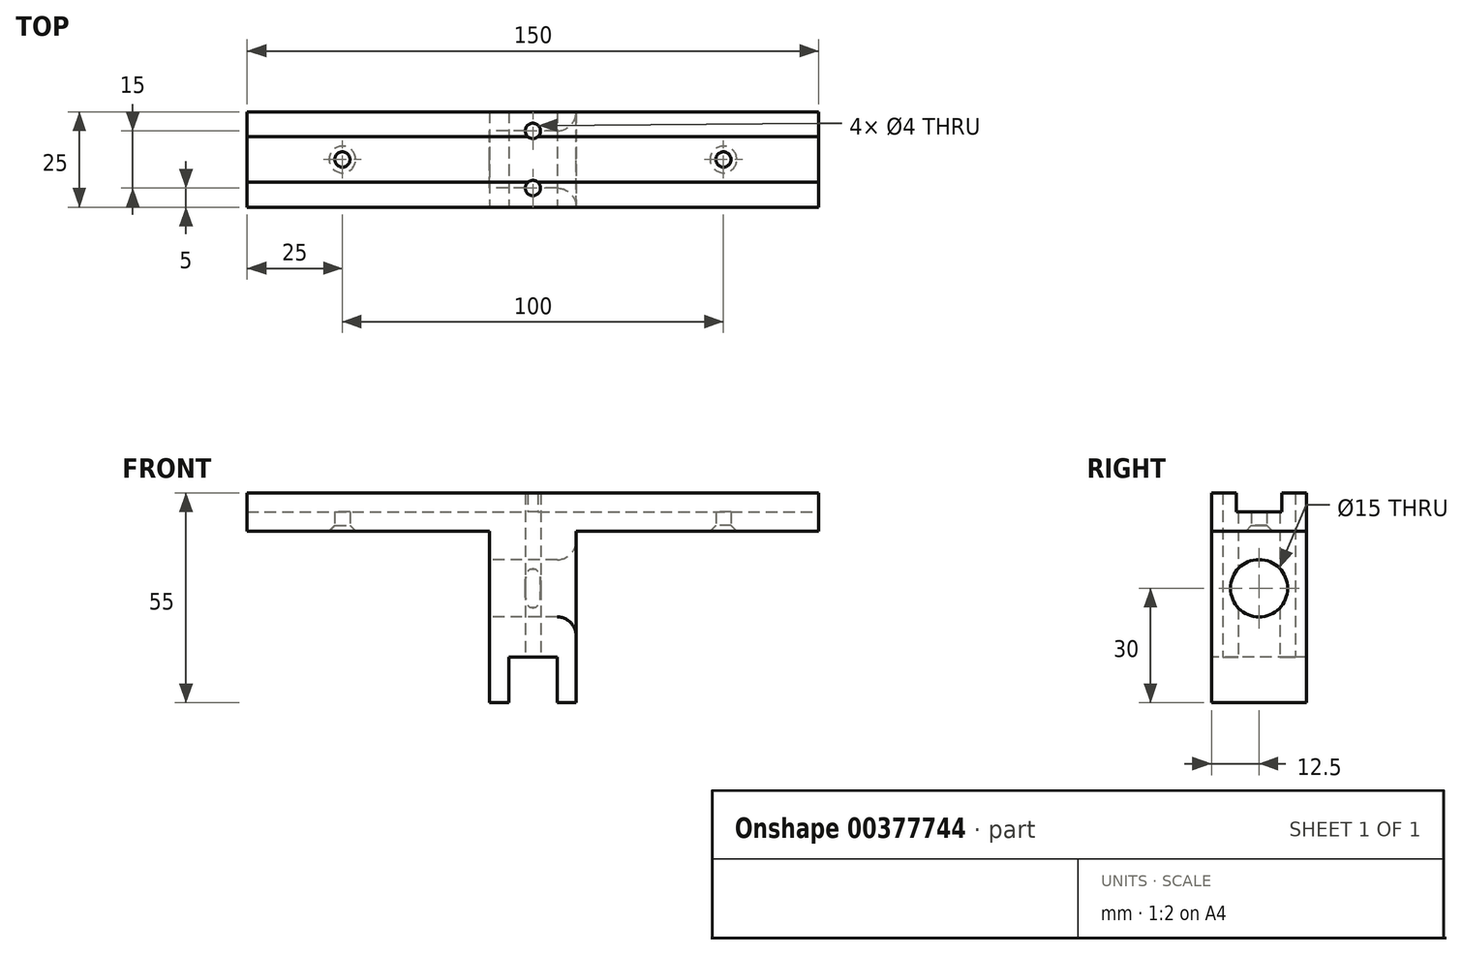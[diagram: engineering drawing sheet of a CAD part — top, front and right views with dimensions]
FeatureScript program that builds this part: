
annotation { "Feature Type Name" : "Feature", "Feature Type Description" : "" }
export const myFeature = defineFeature(function(context is Context, id is Id, definition is map)
    precondition{}
    {
        {
            var Q0;
            Q0=qCreatedBy(makeId("Top.planeOp"),FACE);
            var sketch = newSketch(context, id + "F0", { "sketchPlane" : qUnion([Q0])});
            skLineSegment(sketch, "E0.bottom", {"start": v(75, -12.5) * mm, "end": v(-75, -12.5) * mm});
            skLineSegment(sketch, "E0.top", {"start": v(75, 12.5) * mm, "end": v(-75, 12.5) * mm});
            skLineSegment(sketch, "E0.left", {"start": v(75, -12.5) * mm, "end": v(75, 12.5) * mm});
            skLineSegment(sketch, "E0.right", {"start": v(-75, -12.5) * mm, "end": v(-75, 12.5) * mm});
            skPoint(sketch, "E0.middle", {"position": v(0, 0) * mm});
            skLineSegment(sketch, "E1", {"start": v(0, 0) * mm, "end": v(0, 7.5) * mm, "construction": true});
            skCircle(sketch, "E2", {"center": v(0, 7.5) * mm, "radius": 2 * mm});
            skCircle(sketch, "E3.MirrorC", {"center": v(0, -7.5) * mm, "radius": 2 * mm});
            skLineSegment(sketch, "E4", {"start": v(0, 0) * mm, "end": v(50, 0) * mm, "construction": true});
            skCircle(sketch, "E5", {"center": v(50, 0) * mm, "radius": 2 * mm});
            skCircle(sketch, "E6.MirrorC", {"center": v(-50, 0) * mm, "radius": 2 * mm});
            skSolve(sketch);
        }
        {
            var Q0;
            Q0 = qSketchRegion(id + "F0", true);
            extrude(context, id + "F1", {"entities" : qUnion([Q0]), "depth" : 55 * mm});
        }
        {
            var Q0;
            Q0=makeQuery(id+"F1.opExtrude","SWEPT_FACE",FACE,{"disambiguationData":[OSD([sQuery(id+"F0.wireOp",EDGE,"E0.left")])]});
            var sketch = newSketch(context, id + "F2", { "sketchPlane" : qUnion([Q0])});
            skPoint(sketch, "E7.endSnap0", {"position": v(0, 55) * mm});
            skLineSegment(sketch, "E8", {"start": v(0, 55) * mm, "end": v(0, 50) * mm, "construction": true});
            skLineSegment(sketch, "E9", {"start": v(0, 50) * mm, "end": v(6, 50) * mm, "construction": true});
            skLineSegment(sketch, "E10.MirrorCS", {"start": v(0, 50) * mm, "end": v(-6, 50) * mm, "construction": true});
            skLineSegment(sketch, "E11.bottom", {"start": v(6, 50) * mm, "end": v(-6, 50) * mm});
            skLineSegment(sketch, "E11.top", {"start": v(6, 55) * mm, "end": v(-6, 55) * mm});
            skLineSegment(sketch, "E11.left", {"start": v(6, 50) * mm, "end": v(6, 55) * mm});
            skLineSegment(sketch, "E11.right", {"start": v(-6, 50) * mm, "end": v(-6, 55) * mm});
            skSolve(sketch);
        }
        {
            var Q0;
            Q0=makeQuery(id+"F2.imprint","IMPRINT",FACE,{"disambiguationData":[TD([[makeQuery(id+"F2.imprint","IMPRINT",EDGE,{"derivedFrom":sQuery(id+"F2.wireOp",EDGE,"E11.bottom")}),-1.0]])]});
            extrude(context, id + "F3", {"entities" : qUnion([Q0]), "operationType" : NewBodyOperationType.REMOVE, "endBound" : BoundingType.THROUGH_ALL, "oppositeDirection" : true, "depth" : 25 * mm});
        }
        {
            var Q0;
            Q0=makeQuery(id+"F1.opExtrude","SWEPT_FACE",FACE,{"disambiguationData":[OSD([sQuery(id+"F0.wireOp",EDGE,"E0.bottom")])]});
            var sketch = newSketch(context, id + "F4", { "sketchPlane" : qUnion([Q0])});
            skLineSegment(sketch, "E12", {"start": v(0, 0) * mm, "end": v(0, 12) * mm, "construction": true});
            skLineSegment(sketch, "E13", {"start": v(0, 12) * mm, "end": v(6.35, 12) * mm, "construction": true});
            skLineSegment(sketch, "E14.MirrorCS", {"start": v(0, 12) * mm, "end": v(-6.35, 12) * mm, "construction": true});
            skLineSegment(sketch, "E15.bottom", {"start": v(-6.35, 12) * mm, "end": v(6.35, 12) * mm});
            skLineSegment(sketch, "E15.top", {"start": v(-6.35, 0) * mm, "end": v(6.35, 0) * mm});
            skLineSegment(sketch, "E15.left", {"start": v(-6.35, 12) * mm, "end": v(-6.35, 0) * mm});
            skLineSegment(sketch, "E15.right", {"start": v(6.35, 12) * mm, "end": v(6.35, 0) * mm});
            skLineSegment(sketch, "E16", {"start": v(-75, 55) * mm, "end": v(-75, 45) * mm, "construction": true});
            skLineSegment(sketch, "E17", {"start": v(-6.35, 0) * mm, "end": v(-11.35, 0) * mm, "construction": true});
            skLineSegment(sketch, "E18.bottom", {"start": v(-75, 45) * mm, "end": v(-11.35, 45) * mm});
            skLineSegment(sketch, "E18.top", {"start": v(-75, 0) * mm, "end": v(-11.35, 0) * mm});
            skLineSegment(sketch, "E18.left", {"start": v(-75, 45) * mm, "end": v(-75, 0) * mm});
            skLineSegment(sketch, "E18.right", {"start": v(-11.35, 45) * mm, "end": v(-11.35, 0) * mm});
            skLineSegment(sketch, "E19.MirrorCS", {"start": v(75, 45) * mm, "end": v(75, 0) * mm});
            skLineSegment(sketch, "E20.MirrorCS", {"start": v(75, 45) * mm, "end": v(11.35, 45) * mm});
            skLineSegment(sketch, "E21.MirrorCS", {"start": v(11.35, 45) * mm, "end": v(11.35, 0) * mm});
            skLineSegment(sketch, "E22.MirrorCS", {"start": v(75, 0) * mm, "end": v(11.35, 0) * mm});
            skSolve(sketch);
        }
        {
            var Q0;
            Q0=makeQuery(id+"F4.imprint","IMPRINT",FACE,{"disambiguationData":[TD([[makeQuery(id+"F4.imprint","IMPRINT",EDGE,{"derivedFrom":sQuery(id+"F4.wireOp",EDGE,"E19.MirrorCS")}),-1.0]])]});
            var Q1;
            Q1=makeQuery(id+"F4.imprint","IMPRINT",FACE,{"disambiguationData":[TD([[makeQuery(id+"F4.imprint","IMPRINT",EDGE,{"derivedFrom":sQuery(id+"F4.wireOp",EDGE,"E18.bottom")}),-1.0]])]});
            var Q2;
            Q2=makeQuery(id+"F4.imprint","IMPRINT",FACE,{"disambiguationData":[TD([[makeQuery(id+"F4.imprint","IMPRINT",EDGE,{"derivedFrom":sQuery(id+"F4.wireOp",EDGE,"E15.bottom")}),-1.0]])]});
            extrude(context, id + "F5", {"entities" : qUnion([Q0, Q1, Q2]), "operationType" : NewBodyOperationType.REMOVE, "endBound" : BoundingType.THROUGH_ALL, "oppositeDirection" : true, "depth" : 25 * mm});
        }
        {
            var Q0;
            Q0=makeQuery(id+"F5.boolean.opBoolean","COPY",FACE,{"derivedFrom":makeQuery(id+"F5.opExtrude","SWEPT_FACE",FACE,{"disambiguationData":[OSD([sQuery(id+"F4.wireOp",EDGE,"E18.right")])]})});
            var sketch = newSketch(context, id + "F6", { "sketchPlane" : qUnion([Q0])});
            skCircle(sketch, "E23", {"center": v(0, 0) * mm, "radius": 7.5 * mm});
            skLineSegment(sketch, "E24", {"start": v(0, 0) * mm, "end": v(0, 30) * mm, "construction": true});
            skCircle(sketch, "E25", {"center": v(0, 30) * mm, "radius": 7.5 * mm});
            skSolve(sketch);
        }
        {
            var Q0;
            {var subQ0=sQuery(id+"F6.wireOp",EDGE,"E23");var subQ1=makeQuery(id+"F5.boolean.opBoolean","COPY",EDGE,{"derivedFrom":makeQuery(id+"F5.opExtrude","SWEPT_EDGE",EDGE,{"disambiguationData":[OSD([sQuery(id+"F0.wireOp",EDGE,"E0.bottom"),sQuery(id+"F4.wireOp",EDGE,"E18.top"),sQuery(id+"F4.wireOp",EDGE,"E18.right")])]})});var subQ2=makeQuery(id+"F6.imprint","INTERSECT",VERTEX,{"disambiguationData":[OD(0.0)],"derivedFrom":[subQ1,subQ0]});Q0=makeQuery(id+"F6.imprint","IMPRINT",FACE,{"disambiguationData":[TD([[makeQuery(id+"F6.imprint","IMPRINT",EDGE,{"disambiguationData":[TD([[subQ2,-1.0]])],"derivedFrom":subQ0}),1.0]])]});}
            extrude(context, id + "F7", {"entities" : qUnion([Q0]), "operationType" : NewBodyOperationType.REMOVE, "endBound" : BoundingType.THROUGH_ALL, "oppositeDirection" : true, "depth" : 25 * mm});
        }
        {
            var Q0;
            Q0=makeQuery(id+"F6.imprint","IMPRINT",FACE,{"disambiguationData":[TD([[makeQuery(id+"F6.imprint","IMPRINT",EDGE,{"derivedFrom":sQuery(id+"F6.wireOp",EDGE,"E25")}),1.0]])]});
            extrude(context, id + "F8", {"entities" : qUnion([Q0]), "operationType" : NewBodyOperationType.REMOVE, "endBound" : BoundingType.THROUGH_ALL, "oppositeDirection" : true, "depth" : 25 * mm});
        }
        {
            var Q0;
            Q0=makeQuery(id+"F8.boolean.opBoolean","COPY",EDGE,{"derivedFrom":makeQuery(id+"F8.opExtrude","CAP_EDGE",EDGE,{"disambiguationData":[OSD([sQuery(id+"F6.wireOp",EDGE,"E25")])],"isStart":true})});
            var Q1;
            Q1=makeQuery(id+"F8.boolean.opBoolean","INTERSECT",EDGE,{"derivedFrom":[makeQuery(id+"F5.boolean.opBoolean","COPY",FACE,{"derivedFrom":makeQuery(id+"F5.opExtrude","SWEPT_FACE",FACE,{"disambiguationData":[OSD([sQuery(id+"F4.wireOp",EDGE,"E21.MirrorCS")])]})}),makeQuery(id+"F8.opExtrude","SWEPT_FACE",FACE,{"disambiguationData":[OSD([sQuery(id+"F6.wireOp",EDGE,"E25")])]})]});
            fillet(context, id + "F9", {"entities" : qUnion([Q0, Q1]), "radius" : 5 * mm, "tangentPropagation" : true, "allowEdgeOverflow" : false});
        }
        {
            var Q0;
            Q0=makeQuery(id+"F5.boolean.opBoolean","INTERSECT",EDGE,{"derivedFrom":[makeQuery(id+"F1.opExtrude","SWEPT_FACE",FACE,{"disambiguationData":[OSD([sQuery(id+"F0.wireOp",EDGE,"E5")])]}),makeQuery(id+"F5.opExtrude","SWEPT_FACE",FACE,{"disambiguationData":[OSD([sQuery(id+"F4.wireOp",EDGE,"E20.MirrorCS")])]})]});
            var Q1;
            Q1=makeQuery(id+"F5.boolean.opBoolean","INTERSECT",EDGE,{"derivedFrom":[makeQuery(id+"F1.opExtrude","SWEPT_FACE",FACE,{"disambiguationData":[OSD([sQuery(id+"F0.wireOp",EDGE,"E6.MirrorC")])]}),makeQuery(id+"F5.opExtrude","SWEPT_FACE",FACE,{"disambiguationData":[OSD([sQuery(id+"F4.wireOp",EDGE,"E18.bottom")])]})]});
            chamfer(context, id + "F10", {"entities" : qUnion([Q0, Q1]), "width" : 1.5 * mm, "tangentPropagation" : true});
        }
    });
